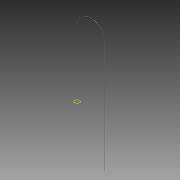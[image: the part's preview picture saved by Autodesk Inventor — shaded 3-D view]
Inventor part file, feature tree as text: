
AUTODESK INVENTOR PART (.ipt)
format: ipt  version: 2012 SP2 (Build 160219200, 219)  size: 75,264 bytes
history: native  units: in
note: dims shown in document units (in); Inventor stores cm internally (conversion verified against a paired STEP export)
features: sketch x2, reference x2, plane x1, sweep x1
ambient origin geometry x8: Origin, YZ Plane, XZ Plane, XY Plane, X Axis, Y Axis, Z Axis, Center Point
feature tree (6):
  sketch  "Sketch1"  dims[d0=11.811in d2=0.0315in]
  plane  "Work Plane1"
  sweep  "Sweep2"
  reference  "Reference1"
  reference  "Reference2"
  sketch  "Sketch2"  dims[d3=1.3701in d6=23.622in d7=0.0in]
